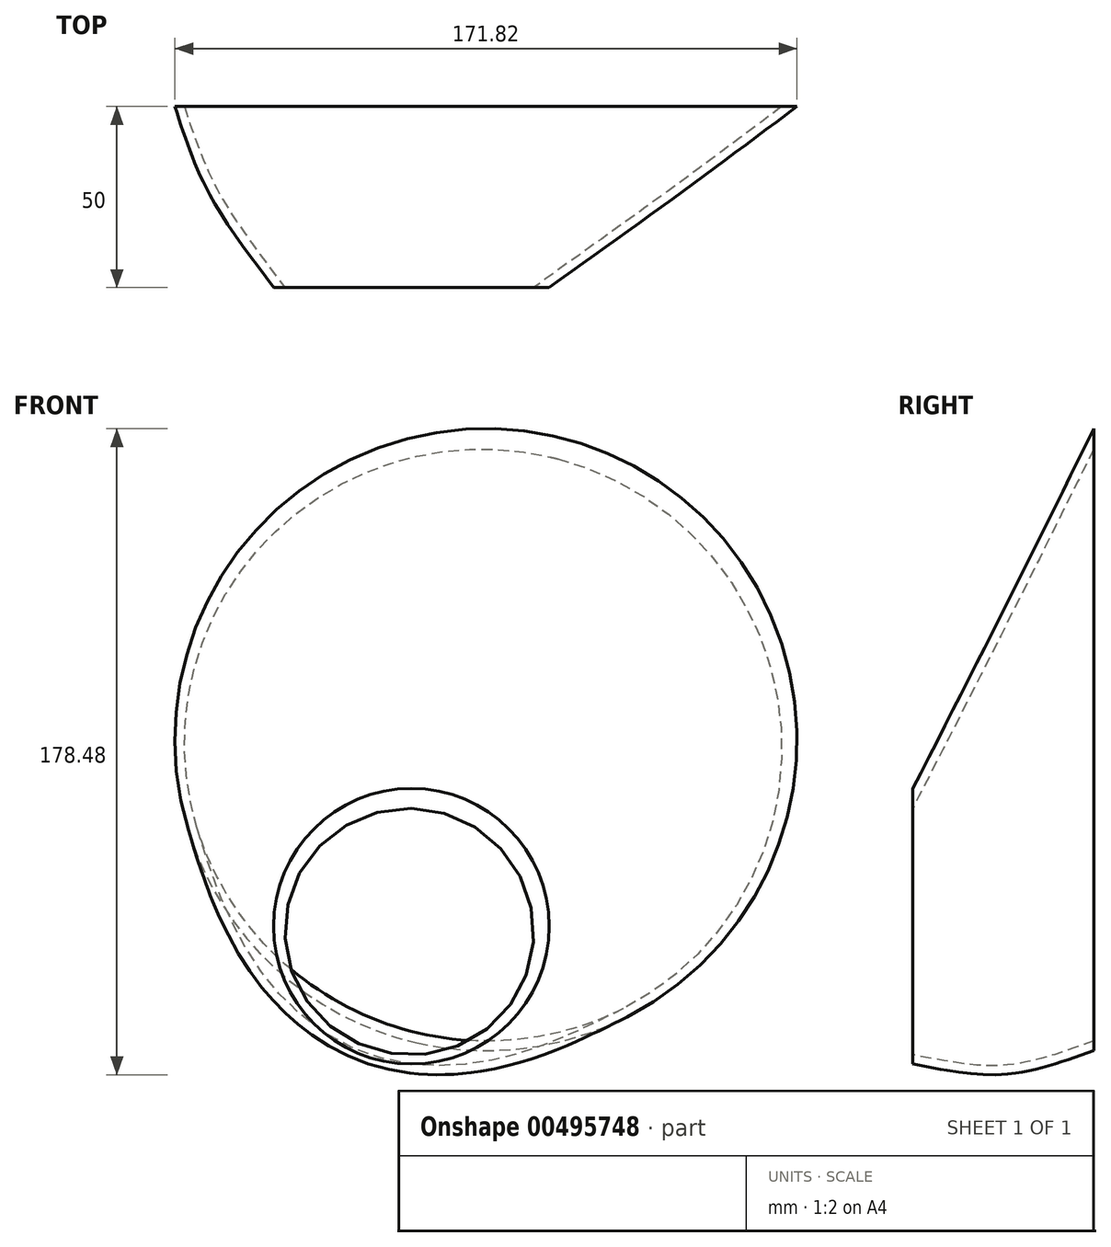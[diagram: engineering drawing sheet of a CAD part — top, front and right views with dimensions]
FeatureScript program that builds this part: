
annotation { "Feature Type Name" : "Feature", "Feature Type Description" : "" }
export const myFeature = defineFeature(function(context is Context, id is Id, definition is map)
    precondition{}
    {
        {
            var Q0;
            Q0=qCreatedBy(makeId("Front.planeOp"),FACE);
            cPlane(context, id + "F0", {"entities" : qUnion([Q0]), "cplaneType" : CPlaneType.OFFSET, "offset" : 25 * mm, "width" : 150 * mm, "height" : 150 * mm});
        }
        {
            var Q0;
            Q0=qCreatedBy(id+"F0.planeOp",FACE);
            cPlane(context, id + "F1", {"entities" : qUnion([Q0]), "cplaneType" : CPlaneType.OFFSET, "offset" : 25 * mm, "width" : 150 * mm, "height" : 150 * mm});
        }
        {
            var Q0;
            Q0=qCreatedBy(makeId("Front.planeOp"),FACE);
            var sketch = newSketch(context, id + "F2", { "sketchPlane" : qUnion([Q0])});
            skCircle(sketch, "E0", {"center": v(0, 0) * mm, "radius": 85.9 * mm});
            skSolve(sketch);
        }
        {
            var Q0;
            Q0=qCreatedBy(id+"F0.planeOp",FACE);
            var sketch = newSketch(context, id + "F3", { "sketchPlane" : qUnion([Q0])});
            skCircle(sketch, "E1", {"center": v(-11.85, -28.4) * mm, "radius": 64.08 * mm});
            skSolve(sketch);
        }
        {
            var Q0;
            Q0=qCreatedBy(id+"F1.planeOp",FACE);
            var sketch = newSketch(context, id + "F4", { "sketchPlane" : qUnion([Q0])});
            skCircle(sketch, "E2", {"center": v(-20.6, -51.56) * mm, "radius": 38.07 * mm});
            skSolve(sketch);
        }
        {
            var Q0;
            Q0=makeQuery(id+"F4.imprint","IMPRINT",FACE,{"disambiguationData":[TD([[makeQuery(id+"F4.imprint","IMPRINT",EDGE,{"derivedFrom":sQuery(id+"F4.wireOp",EDGE,"E2")}),1.0]])]});
            var Q1;
            Q1=makeQuery(id+"F3.imprint","IMPRINT",FACE,{"disambiguationData":[TD([[makeQuery(id+"F3.imprint","IMPRINT",EDGE,{"derivedFrom":sQuery(id+"F3.wireOp",EDGE,"E1")}),1.0]])]});
            var Q2;
            Q2=makeQuery(id+"F2.imprint","IMPRINT",FACE,{"disambiguationData":[TD([[makeQuery(id+"F2.imprint","IMPRINT",EDGE,{"derivedFrom":sQuery(id+"F2.wireOp",EDGE,"E0")}),1.0]])]});
            loft(context, id + "F5", {"sheetProfilesArray" : [{ "sheetProfileEntities" : qUnion([Q0]) }, { "sheetProfileEntities" : qUnion([Q1]) }, { "sheetProfileEntities" : qUnion([Q2]) }]});
        }
        {
            var Q0;
            Q0=makeQuery(id+"F5.opLoft","CAP_FACE",FACE,{"disambiguationData":[OSD([makeQuery(id+"F4.imprint","IMPRINT",FACE,{"disambiguationData":[TD([[makeQuery(id+"F4.imprint","IMPRINT",EDGE,{"derivedFrom":sQuery(id+"F4.wireOp",EDGE,"E2")}),1.0]])]})])],"isStart":true});
            var Q1;
            Q1=makeQuery(id+"F5.opLoft","CAP_FACE",FACE,{"disambiguationData":[OSD([makeQuery(id+"F2.imprint","IMPRINT",FACE,{"disambiguationData":[TD([[makeQuery(id+"F2.imprint","IMPRINT",EDGE,{"derivedFrom":sQuery(id+"F2.wireOp",EDGE,"E0")}),1.0]])]})])],"isStart":true});
            shell(context, id + "F6", {"entities" : qUnion([Q0, Q1]), "thickness" : 2.5 * mm});
        }
    });
